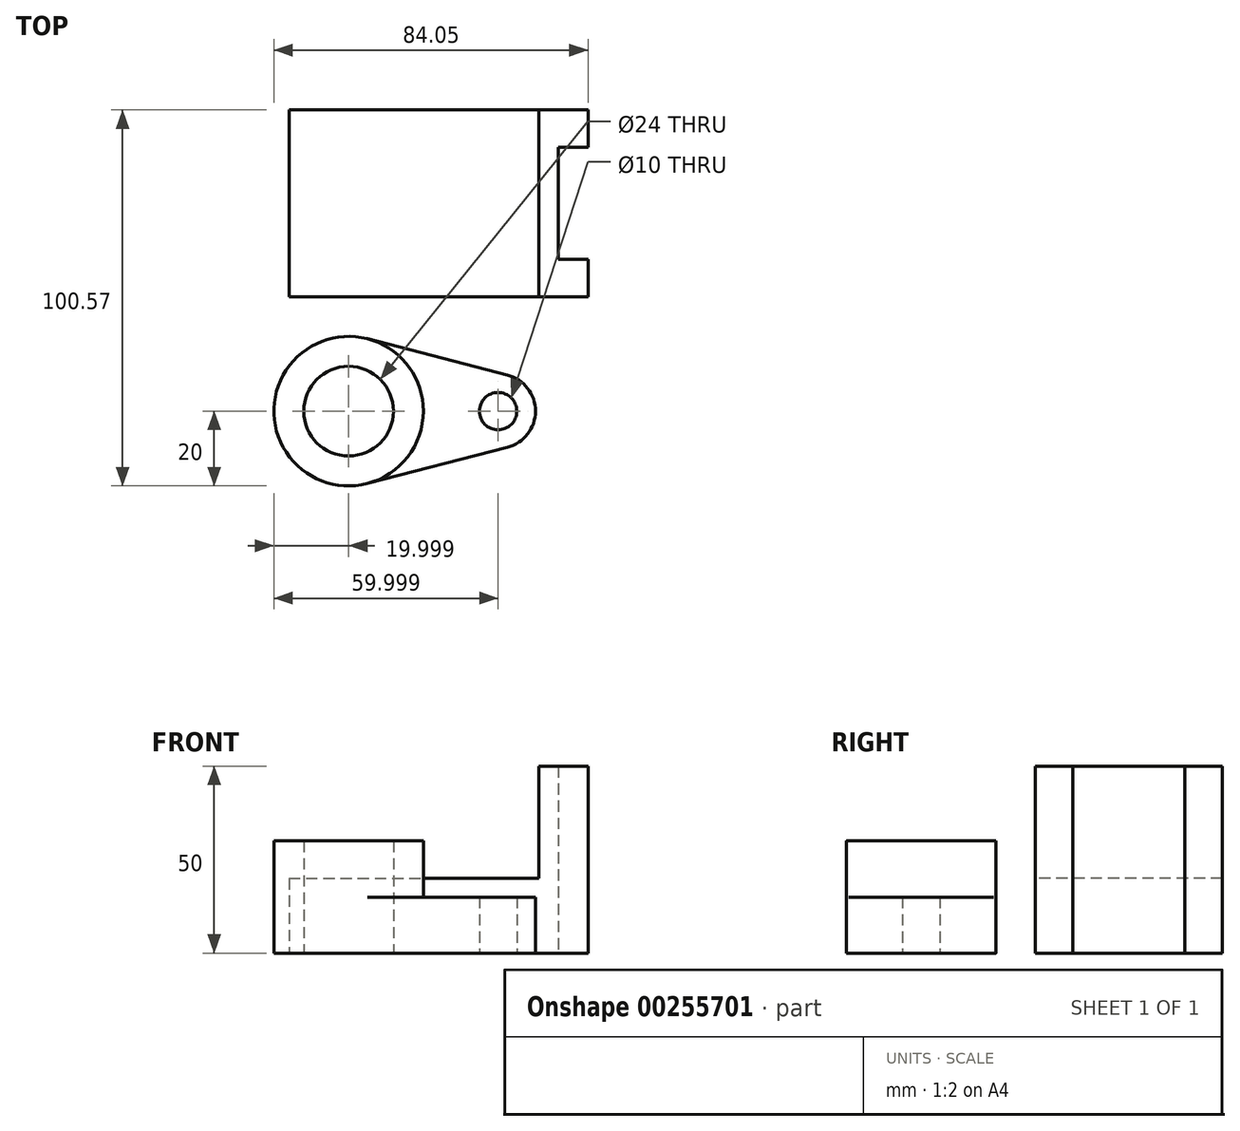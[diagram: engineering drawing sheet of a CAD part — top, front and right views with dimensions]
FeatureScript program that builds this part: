
annotation { "Feature Type Name" : "Feature", "Feature Type Description" : "" }
export const myFeature = defineFeature(function(context is Context, id is Id, definition is map)
    precondition{}
    {
        {
            var Q0;
            Q0=qCreatedBy(makeId("Top.planeOp"),FACE);
            var sketch = newSketch(context, id + "F0", { "sketchPlane" : qUnion([Q0])});
            skLineSegment(sketch, "E0.bottom", {"start": v(-38.51, 36.43) * mm, "end": v(28.3, 36.43) * mm});
            skLineSegment(sketch, "E0.top", {"start": v(-38.51, -13.57) * mm, "end": v(28.3, -13.57) * mm});
            skLineSegment(sketch, "E0.left", {"start": v(-38.51, 36.43) * mm, "end": v(-38.51, -13.57) * mm});
            skLineSegment(sketch, "E0.right", {"start": v(28.3, 36.43) * mm, "end": v(28.3, -13.57) * mm});
            skLineSegment(sketch, "E1.bottom", {"start": v(28.3, 36.43) * mm, "end": v(41.49, 36.43) * mm});
            skLineSegment(sketch, "E1.top", {"start": v(28.3, -13.57) * mm, "end": v(41.49, -13.57) * mm});
            skLineSegment(sketch, "E1.right", {"start": v(41.49, 36.43) * mm, "end": v(41.49, 26.43) * mm});
            skLineSegment(sketch, "E2.bottom", {"start": v(41.49, 26.43) * mm, "end": v(33.49, 26.43) * mm});
            skLineSegment(sketch, "E2.top", {"start": v(41.49, -3.57) * mm, "end": v(33.49, -3.57) * mm});
            skLineSegment(sketch, "E2.right", {"start": v(33.49, 26.43) * mm, "end": v(33.49, -3.57) * mm});
            skLineSegment(sketch, "E3.trimOffspring", {"start": v(41.49, -3.57) * mm, "end": v(41.49, -13.57) * mm});
            skSolve(sketch);
        }
        {
            var Q0;
            Q0=makeQuery(id+"F0.imprint","IMPRINT",FACE,{"disambiguationData":[TD([[makeQuery(id+"F0.imprint","IMPRINT",EDGE,{"derivedFrom":sQuery(id+"F0.wireOp",EDGE,"E0.bottom")}),-1.0]])]});
            extrude(context, id + "F1", {"entities" : qUnion([Q0]), "depth" : 20 * mm});
        }
        {
            var Q0;
            Q0=makeQuery(id+"F0.imprint","IMPRINT",FACE,{"disambiguationData":[TD([[makeQuery(id+"F0.imprint","IMPRINT",EDGE,{"derivedFrom":sQuery(id+"F0.wireOp",EDGE,"E1.bottom")}),-1.0]])]});
            extrude(context, id + "F2", {"entities" : qUnion([Q0]), "operationType" : NewBodyOperationType.ADD, "depth" : 50 * mm});
        }
        {
            var Q0;
            Q0=qCreatedBy(makeId("Top.planeOp"),FACE);
            var sketch = newSketch(context, id + "F3", { "sketchPlane" : qUnion([Q0])});
            skCircle(sketch, "E4", {"center": v(-22.56, -44.14) * mm, "radius": 12 * mm});
            skCircle(sketch, "E5", {"center": v(-22.56, -44.14) * mm, "radius": 20 * mm});
            skArc(sketch, "E6", {"start": v(19.94, -53.82) * mm, "mid": v(27.44, -44.14) * mm, "end": v(19.94, -34.46) * mm});
            skLineSegment(sketch, "E7", {"start": v(-17.56, -24.77) * mm, "end": v(19.94, -34.46) * mm});
            skLineSegment(sketch, "E8", {"start": v(-17.56, -63.5) * mm, "end": v(19.94, -53.82) * mm});
            skCircle(sketch, "E9", {"center": v(17.44, -44.14) * mm, "radius": 5 * mm});
            skSolve(sketch);
        }
        {
            var Q0;
            Q0=makeQuery(id+"F3.imprint","IMPRINT",FACE,{"disambiguationData":[TD([[makeQuery(id+"F3.imprint","IMPRINT",EDGE,{"derivedFrom":sQuery(id+"F3.wireOp",EDGE,"E4")}),-1.0]])]});
            extrude(context, id + "F4", {"entities" : qUnion([Q0]), "depth" : 30 * mm});
        }
        {
            var Q0;
            Q0=makeQuery(id+"F3.imprint","IMPRINT",FACE,{"disambiguationData":[TD([[makeQuery(id+"F3.imprint","IMPRINT",EDGE,{"derivedFrom":sQuery(id+"F3.wireOp",EDGE,"E6")}),1.0]])]});
            extrude(context, id + "F5", {"entities" : qUnion([Q0]), "operationType" : NewBodyOperationType.ADD, "depth" : 15 * mm});
        }
    });
